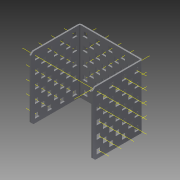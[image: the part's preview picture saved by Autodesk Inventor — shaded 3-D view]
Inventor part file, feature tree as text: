
AUTODESK INVENTOR PART (.ipt)
format: ipt  version: 2015 SP1 (Build 190203100, 203)  size: 613,376 bytes
history: native  units: in
note: dims shown in document units (in); Inventor stores cm internally (conversion verified against a paired STEP export)
features: other x113, pattern_linear x4, imported_body x1
ambient origin geometry x8: Origin, YZ Plane, XZ Plane, XY Plane, X Axis, Y Axis, Z Axis, Center Point
bodies: Body1 (feature_tree)
feature tree (118):
  other  "LPattern4"
  other  "276-1546-001 Rev21"
  other  "Work Point1"
  other  "Work Point2"
  other  "Work Point3"
  other  "Work Point4"
  other  "Work Point5"
  other  "Work Point6"
  other  "Work Axis1"
  other  "Work Axis2"
  other  "Work Axis3"
  other  "Work Axis4"
  other  "Work Axis5"
  other  "Work Axis6"
  pattern_linear  "Rectangular Pattern1"  Count1=4 Spacing1=0.5in
  pattern_linear  "Rectangular Pattern2"  Count1=3 Spacing1=0.5in
  pattern_linear  "Rectangular Pattern3"  Count1=5 Spacing1=0.5in
  pattern_linear  "Rectangular Pattern4"  Count1=5 Spacing1=0.5in
  imported_body  "Base1"
  other  "Work Axis7"
  other  "Work Axis8"
  other  "Work Axis9"
  other  "Work Axis10"
  other  "Work Axis11"
  other  "Work Axis12"
  other  "Work Axis13"
  other  "Work Axis14"
  other  "Work Axis15"
  other  "Work Axis16"
  other  "Work Axis17"
  other  "Work Axis18"
  other  "Work Axis19"
  other  "Work Axis20"
  other  "Work Axis21"
  other  "Work Axis22"
  other  "Work Axis23"
  other  "Work Axis24"
  other  "Work Axis25"
  other  "Work Axis26"
  other  "Work Axis27"
  other  "Work Axis28"
  other  "Work Axis29"
  other  "Work Axis30"
  other  "Work Axis31"
  other  "Work Axis32"
  other  "Work Axis33"
  other  "Work Axis34"
  other  "Work Axis35"
  other  "Work Axis36"
  other  "Work Axis37"
  other  "Work Axis38"
  other  "Work Axis39"
  other  "Work Axis40"
  other  "Work Axis41"
  other  "Work Axis42"
  other  "Work Axis43"
  other  "Work Axis44"
  other  "Work Axis45"
  other  "Work Axis46"
  other  "Work Axis47"
  other  "Work Axis48"
  other  "Work Axis49"
  other  "Work Axis50"
  other  "Work Axis51"
  other  "Work Axis52"
  other  "Work Axis53"
  other  "Work Axis54"
  other  "Work Axis55"
  other  "Work Axis56"
  other  "Work Axis57"
  other  "Work Axis58"
  other  "Work Axis59"
  other  "Work Axis60"
  other  "Work Axis61"
  other  "Work Axis62"
  other  "Work Axis63"
  other  "Work Axis64"
  other  "Work Axis65"
  other  "Work Axis66"
  other  "Work Axis67"
  other  "Work Axis68"
  other  "Work Axis69"
  other  "Work Axis70"
  other  "Work Axis71"
  other  "Work Axis72"
  other  "Work Axis73"
  other  "Work Axis74"
  other  "Work Axis75"
  other  "Work Axis76"
  other  "Work Axis77"
  other  "Work Axis78"
  other  "Work Axis79"
  other  "Work Axis80"
  other  "Work Axis81"
  other  "Work Axis82"
  other  "Work Axis83"
  other  "Work Axis84"
  other  "Work Axis85"
  other  "Work Axis86"
  other  "Work Axis87"
  other  "Work Axis88"
  other  "Work Axis89"
  other  "Work Axis90"
  other  "Work Axis91"
  other  "Work Axis92"
  other  "Work Axis93"
  other  "Work Axis94"
  other  "Work Axis95"
  other  "Work Axis96"
  other  "Work Axis97"
  other  "Work Axis98"
  other  "Work Axis99"
  other  "Work Axis100"
  other  "Work Axis101"
  other  "Work Axis102"
  other  "Work Axis103"
  other  "Work Axis104"
  other  "Work Axis105"
